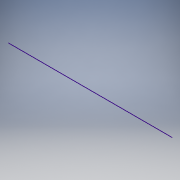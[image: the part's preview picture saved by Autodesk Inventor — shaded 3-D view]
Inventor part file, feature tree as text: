
AUTODESK INVENTOR PART (.ipt)
format: ipt  version: 2018 (Build 220112000, 112)  size: 81,408 bytes
history: native  units: mm
features: sketch x1
ambient origin geometry x8: Origin, YZ Plane, XZ Plane, XY Plane, X Axis, Y Axis, Z Axis, Center Point
feature tree (1):
  sketch  "Sketch1"
